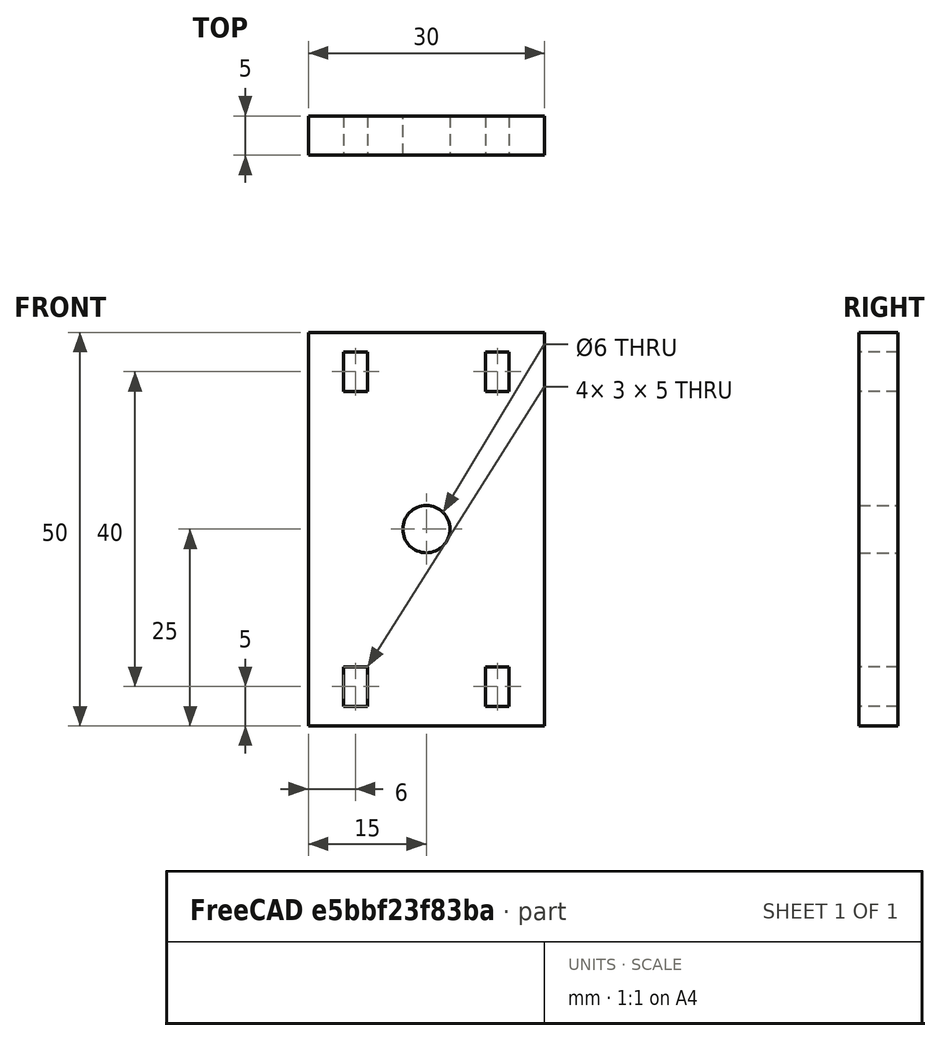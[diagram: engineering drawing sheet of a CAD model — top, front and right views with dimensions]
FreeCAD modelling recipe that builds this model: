
FCSTD DOCUMENT  (FreeCAD 0.16R6712 (Git))
Label: BearingStopAxis
License: All rights reserved
LicenseURL: http://en.wikipedia.org/wiki/All_rights_reserved
objects: Sketcher::SketchObject×1, PartDesign::Pad×1
note: 3 computed .brp shape members not serialized (recipe doc carries the construction recipe); baked Part::Feature solids carry a one-line shape summary decoded from their .brp

FEATURE [Sketcher::SketchObject] Sketch012
  Placement = pos=(0,-5,100) rot=(1,0,0;1.5708rad)
  sketch-geometry (23):
    g0: LineSegment StartX=-15 StartY=25 StartZ=0 EndX=15 EndY=25 EndZ=0
    g1: LineSegment StartX=15 StartY=25 StartZ=0 EndX=15 EndY=-25 EndZ=0
    g2: LineSegment StartX=15 StartY=-25 StartZ=0 EndX=-15 EndY=-25 EndZ=0
    g3: LineSegment StartX=-15 StartY=-25 StartZ=0 EndX=-15 EndY=25 EndZ=0
    g4: LineSegment [constr] StartX=-15 StartY=20 StartZ=0 EndX=15 EndY=20 EndZ=0
    g5: LineSegment StartX=-10.5 StartY=22.5 StartZ=0 EndX=-7.5 EndY=22.5 EndZ=0
    g6: LineSegment StartX=-7.5 StartY=22.5 StartZ=0 EndX=-7.5 EndY=17.5 EndZ=0
    g7: LineSegment StartX=-7.5 StartY=17.5 StartZ=0 EndX=-10.5 EndY=17.5 EndZ=0
    g8: LineSegment StartX=-10.5 StartY=17.5 StartZ=0 EndX=-10.5 EndY=22.5 EndZ=0
    g9: LineSegment StartX=7.5 StartY=22.5 StartZ=0 EndX=10.5 EndY=22.5 EndZ=0
    g10: LineSegment StartX=10.5 StartY=22.5 StartZ=0 EndX=10.5 EndY=17.5 EndZ=0
    g11: LineSegment StartX=10.5 StartY=17.5 StartZ=0 EndX=7.5 EndY=17.5 EndZ=0
    g12: LineSegment StartX=7.5 StartY=17.5 StartZ=0 EndX=7.5 EndY=22.5 EndZ=0
    g13: LineSegment [constr] StartX=-15 StartY=-20 StartZ=0 EndX=15 EndY=-20 EndZ=0
    g14: LineSegment StartX=-10.5 StartY=-17.5 StartZ=0 EndX=-7.5 EndY=-17.5 EndZ=0
    g15: LineSegment StartX=-7.5 StartY=-17.5 StartZ=0 EndX=-7.5 EndY=-22.5 EndZ=0
    g16: LineSegment StartX=-7.5 StartY=-22.5 StartZ=0 EndX=-10.5 EndY=-22.5 EndZ=0
    g17: LineSegment StartX=-10.5 StartY=-22.5 StartZ=0 EndX=-10.5 EndY=-17.5 EndZ=0
    g18: LineSegment StartX=7.5 StartY=-17.5 StartZ=0 EndX=10.5 EndY=-17.5 EndZ=0
    g19: LineSegment StartX=10.5 StartY=-17.5 StartZ=0 EndX=10.5 EndY=-22.5 EndZ=0
    g20: LineSegment StartX=10.5 StartY=-22.5 StartZ=0 EndX=7.5 EndY=-22.5 EndZ=0
    g21: LineSegment StartX=7.5 StartY=-22.5 StartZ=0 EndX=7.5 EndY=-17.5 EndZ=0
    g22: Circle CenterX=0 CenterY=0 CenterZ=0 NormalX=0 NormalY=0 NormalZ=1 Radius=3
  constraints (66):
    c: Coincident(g0,g1)
    c: Coincident(g1,g2)
    c: Coincident(g2,g3)
    c: Coincident(g3,g0)
    c: Horizontal(g0)
    c: Horizontal(g2)
    c: Vertical(g1)
    c: Vertical(g3)
    c: Symmetric(g0,g0,g-2)
    c: Symmetric(g0,g2,g-1)
    c: DistanceX(g0,g0) = 30
    c: DistanceY(g3,g3) = 50
    c: PointOnObject(g4,g3)
    c: PointOnObject(g4,g1)
    c: DistanceY(g4) = 20
    c: Coincident(g5,g6)
    c: Coincident(g6,g7)
    c: Coincident(g7,g8)
    c: Coincident(g8,g5)
    c: Horizontal(g5)
    c: Horizontal(g7)
    c: Vertical(g6)
    c: Vertical(g8)
    c: Coincident(g9,g10)
    c: Coincident(g10,g11)
    c: Coincident(g11,g12)
    c: Coincident(g12,g9)
    c: Horizontal(g9)
    c: Horizontal(g11)
    c: Vertical(g10)
    c: Vertical(g12)
    c: Symmetric(g5,g9,g-2)
    c: Symmetric(g6,g5,g4)
    c: Equal(g6,g12)
    c: Equal(g5,g9)
    c: DistanceY(g8,g8) = 5
    c: DistanceX(g7,g7) = 3
    c: DistanceX(g5,g9) = 15
    c: PointOnObject(g13,g3)
    c: PointOnObject(g13,g1)
    c: Symmetric(g13,g4,g-1)
    c: Coincident(g14,g15)
    c: Coincident(g15,g16)
    c: Coincident(g16,g17)
    c: Coincident(g17,g14)
    c: Horizontal(g14)
    c: Horizontal(g16)
    c: Vertical(g15)
    c: Vertical(g17)
    c: Coincident(g18,g19)
    c: Coincident(g19,g20)
    c: Coincident(g20,g21)
    c: Coincident(g21,g18)
    c: Horizontal(g18)
    c: Horizontal(g20)
    c: Vertical(g19)
    c: Vertical(g21)
    c: Symmetric(g14,g18,g-2)
    c: Symmetric(g15,g14,g13)
    c: Equal(g14,g18)
    c: Equal(g15,g21)
    c: Equal(g17,g8)
    c: Symmetric(g14,g6,g-1)
    c: Equal(g14,g7)
    c: Coincident(g22,g-1)
    c: Radius(g22) = 3
FEATURE [PartDesign::Pad] Pad012  label="TopBearingStop_A"
  Length = 5
  Length2 = 100
  Placement = pos=(0,-5,100) rot=(1,0,0;1.5708rad)
  Sketch = -> Sketch012
  Type = 0
